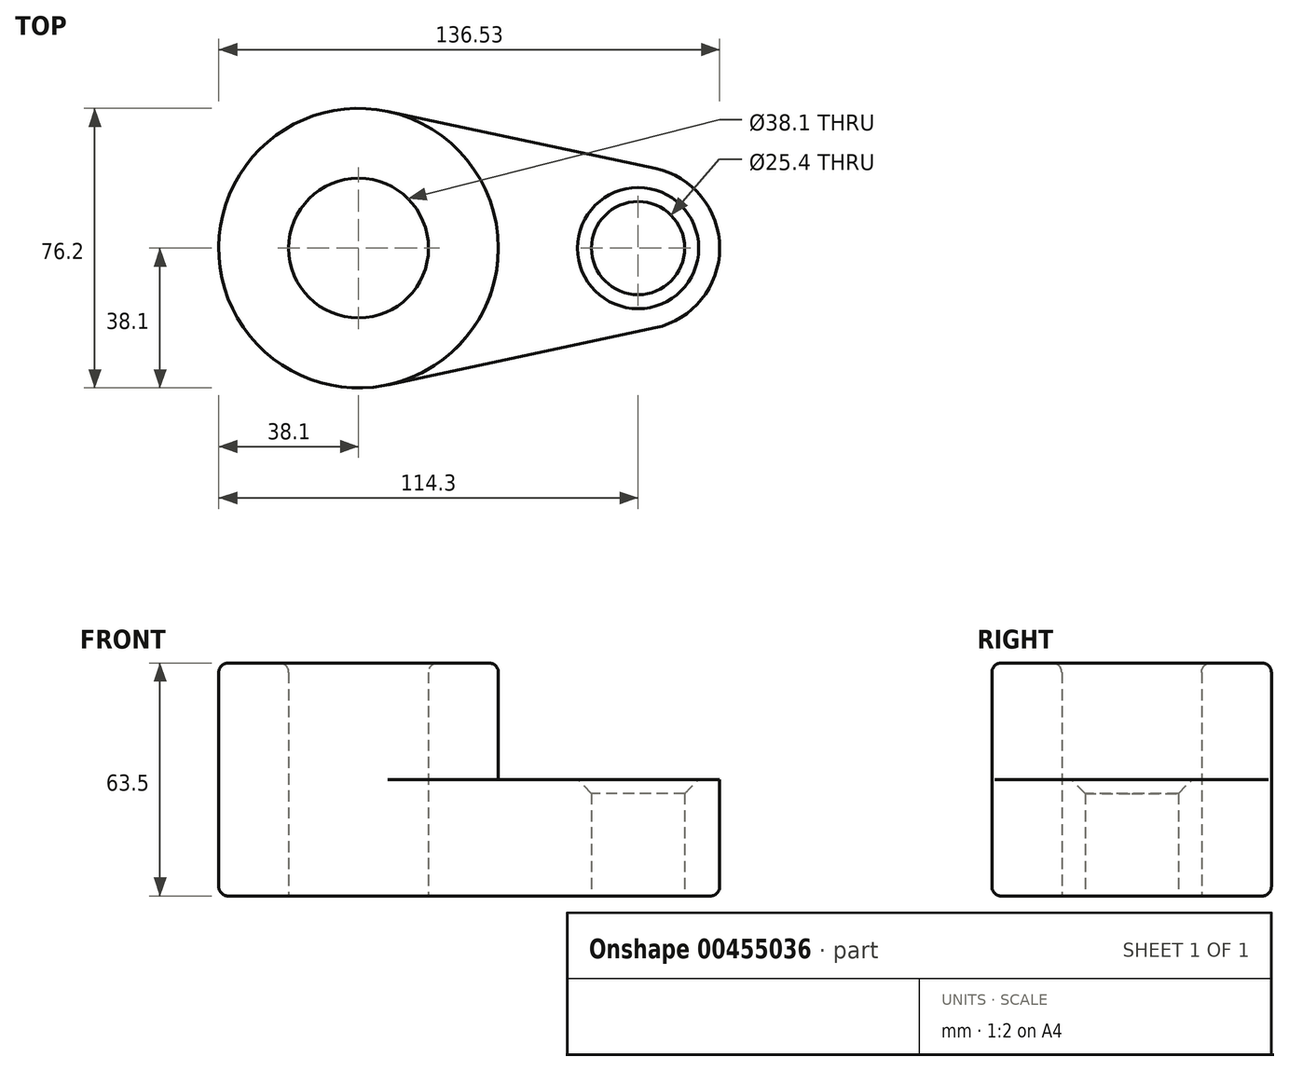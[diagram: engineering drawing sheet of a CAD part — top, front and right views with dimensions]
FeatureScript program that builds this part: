
annotation { "Feature Type Name" : "Feature", "Feature Type Description" : "" }
export const myFeature = defineFeature(function(context is Context, id is Id, definition is map)
    precondition{}
    {
        {
            var Q0;
            Q0=qCreatedBy(makeId("Top.planeOp"),FACE);
            var sketch = newSketch(context, id + "F0", { "sketchPlane" : qUnion([Q0])});
            skCircle(sketch, "E0", {"center": v(0, 0) * mm, "radius": 38.1 * mm});
            skCircle(sketch, "E1", {"center": v(76.2, 0) * mm, "radius": 22.23 * mm});
            skLineSegment(sketch, "E2", {"start": v(7.94, 37.26) * mm, "end": v(80.83, 21.74) * mm});
            skLineSegment(sketch, "E3", {"start": v(7.94, -37.26) * mm, "end": v(80.83, -21.74) * mm});
            skCircle(sketch, "E4", {"center": v(0, 0) * mm, "radius": 19.05 * mm});
            skCircle(sketch, "E5", {"center": v(76.2, 0) * mm, "radius": 12.7 * mm});
            skSolve(sketch);
        }
        {
            var Q0;
            Q0 = qSketchRegion(id + "F0", true);
            extrude(context, id + "F1", {"entities" : qUnion([Q0]), "depth" : 31.75 * mm});
        }
        {
            var Q0;
            Q0=makeQuery(id+"F0.imprint","IMPRINT",FACE,{"disambiguationData":[TD([[makeQuery(id+"F0.imprint","IMPRINT",EDGE,{"derivedFrom":sQuery(id+"F0.wireOp",EDGE,"E4")}),-1.0]])]});
            extrude(context, id + "F2", {"entities" : qUnion([Q0]), "operationType" : NewBodyOperationType.ADD, "depth" : 63.5 * mm});
        }
        {
            var Q0;
            Q0=makeQuery(id+"F2.opExtrude","CAP_FACE",FACE,{"disambiguationData":[OSD([sQuery(id+"F0.wireOp",EDGE,"E0"),sQuery(id+"F0.wireOp",EDGE,"E4")])],"isStart":false});
            var Q1;
            Q1=makeQuery(id+"F1.opExtrude","CAP_EDGE",EDGE,{"disambiguationData":[OSD([sQuery(id+"F0.wireOp",EDGE,"E3")])],"isStart":true});
            fillet(context, id + "F3", {"entities" : qUnion([Q0, Q1]), "radius" : 2.54 * mm, "tangentPropagation" : true, "allowEdgeOverflow" : false});
        }
        {
            var Q0;
            {var subQ0=sQuery(id+"F0.wireOp",EDGE,"E4");Q0=makeQuery(id+"F3.opFillet","BLEND_EDGE",EDGE,{"blendedFrom":[makeQuery(id+"F2.opExtrude","CAP_EDGE",EDGE,{"disambiguationData":[OSD([subQ0])],"isStart":false}),makeQuery(id+"F2.opExtrude","CAP_FACE",FACE,{"disambiguationData":[OSD([sQuery(id+"F0.wireOp",EDGE,"E0"),subQ0])],"isStart":false})],"blendedInto":[makeQuery(id+"F2.opExtrude","CAP_FACE",FACE,{"disambiguationData":[OSD([sQuery(id+"F0.wireOp",EDGE,"E0"),subQ0])],"isStart":false})]});}
            var Q1;
            Q1=makeQuery(id+"F1.opExtrude","CAP_EDGE",EDGE,{"disambiguationData":[OSD([sQuery(id+"F0.wireOp",EDGE,"E5")])],"isStart":false});
            chamfer(context, id + "F4", {"entities" : qUnion([Q0, Q1]), "width" : 3.8 * mm, "tangentPropagation" : true});
        }
    });
